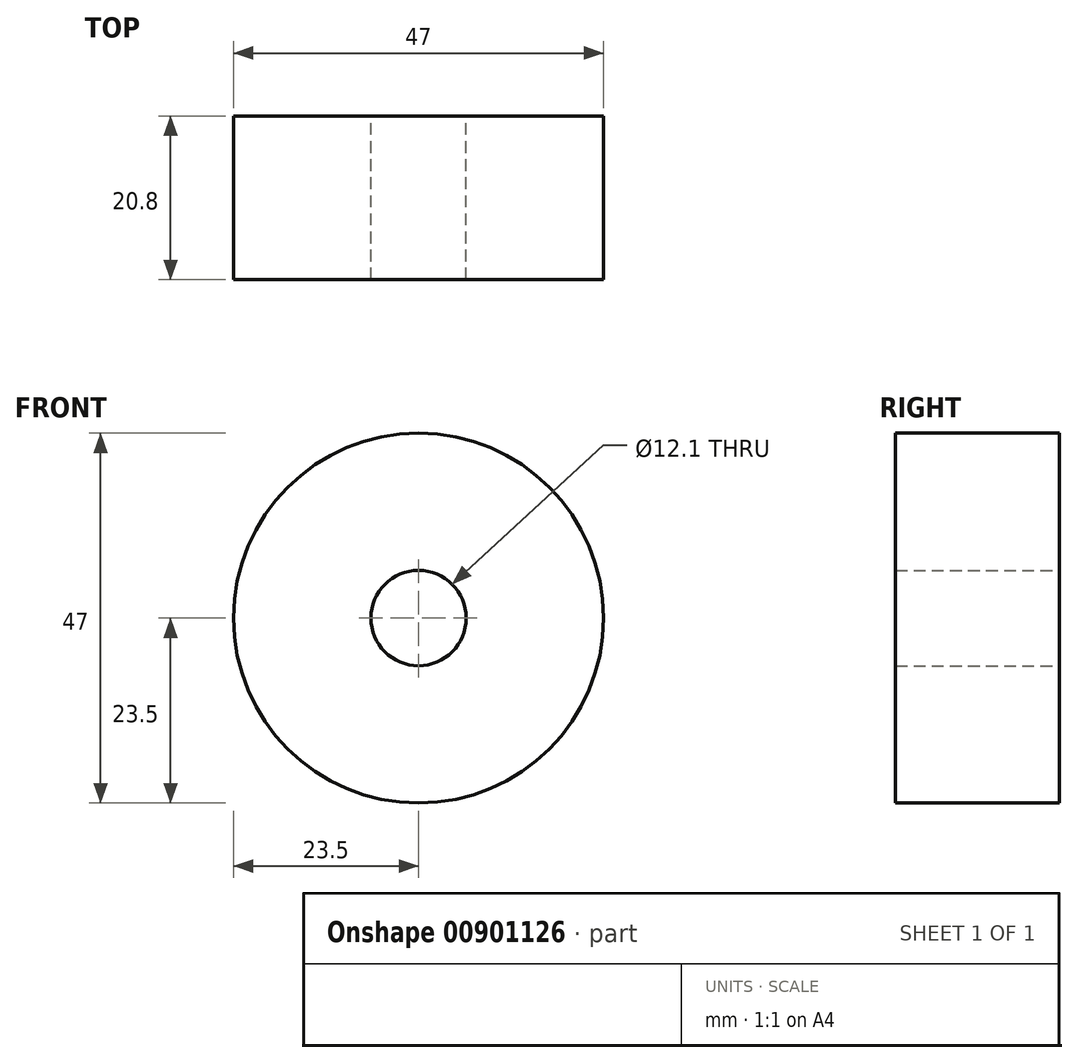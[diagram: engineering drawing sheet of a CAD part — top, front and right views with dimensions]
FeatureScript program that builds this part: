
annotation { "Feature Type Name" : "Feature", "Feature Type Description" : "" }
export const myFeature = defineFeature(function(context is Context, id is Id, definition is map)
    precondition{}
    {
        {
            var Q0;
            Q0=qCreatedBy(makeId("Front.planeOp"),FACE);
            var sketch = newSketch(context, id + "F0", { "sketchPlane" : qUnion([Q0])});
            skCircle(sketch, "E0", {"center": v(0, 0) * mm, "radius": 23.5 * mm});
            skCircle(sketch, "E1", {"center": v(0, 0) * mm, "radius": 6.05 * mm});
            skSolve(sketch);
        }
        {
            var Q0;
            Q0=makeQuery(id+"F0.imprint","IMPRINT",FACE,{"disambiguationData":[TD([[makeQuery(id+"F0.imprint","IMPRINT",EDGE,{"derivedFrom":sQuery(id+"F0.wireOp",EDGE,"E0")}),1.0]])]});
            extrude(context, id + "F1", {"entities" : qUnion([Q0]), "depth" : 20.8 * mm, "offsetDistance" : 25 * mm});
        }
    });
